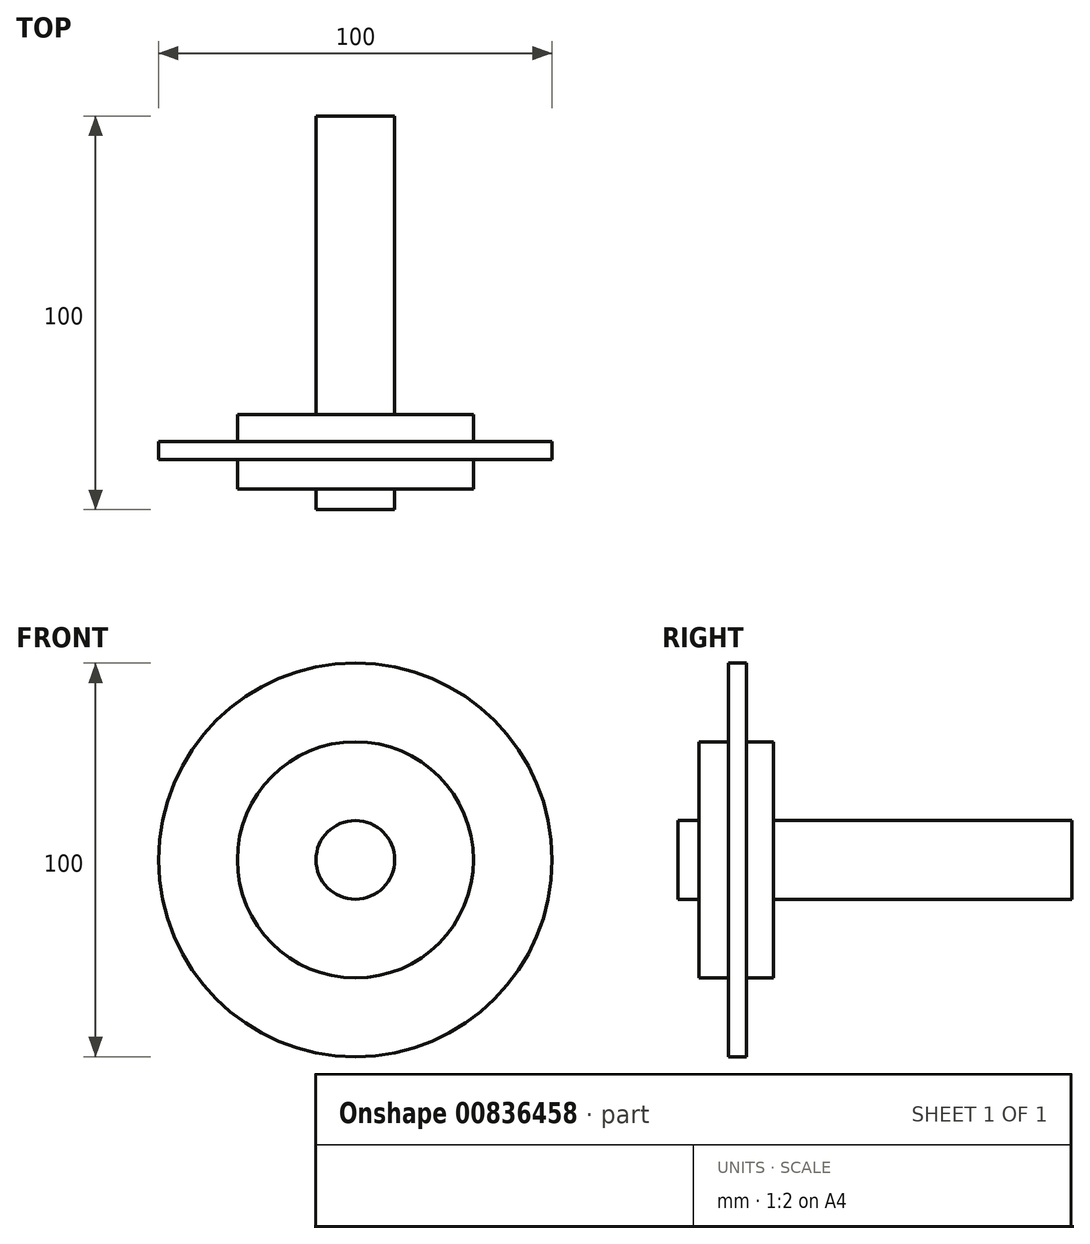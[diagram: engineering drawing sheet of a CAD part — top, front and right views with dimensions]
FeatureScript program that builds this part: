
annotation { "Feature Type Name" : "Feature", "Feature Type Description" : "" }
export const myFeature = defineFeature(function(context is Context, id is Id, definition is map)
    precondition{}
    {
        {
            var Q0;
            Q0=qCreatedBy(makeId("Top.planeOp"),FACE);
            var sketch = newSketch(context, id + "F0", { "sketchPlane" : qUnion([Q0])});
            skLineSegment(sketch, "E0.bottom", {"start": v(0, 0) * mm, "end": v(10, 0) * mm});
            skLineSegment(sketch, "E0.top", {"start": v(0, 100) * mm, "end": v(10, 100) * mm});
            skLineSegment(sketch, "E0.left", {"start": v(0, 0) * mm, "end": v(0, 100) * mm});
            skLineSegment(sketch, "E0.right", {"start": v(10, 0) * mm, "end": v(10, 5.28) * mm});
            skLineSegment(sketch, "E1.bottom", {"start": v(10, 24.16) * mm, "end": v(30, 24.16) * mm});
            skLineSegment(sketch, "E1.top", {"start": v(10, 5.28) * mm, "end": v(30, 5.28) * mm});
            skLineSegment(sketch, "E1.left", {"start": v(0, 24.16) * mm, "end": v(0, 5.28) * mm});
            skLineSegment(sketch, "E1.right", {"start": v(30, 24.16) * mm, "end": v(30, 17.33) * mm});
            skLineSegment(sketch, "E2.bottom", {"start": v(30, 17.33) * mm, "end": v(50, 17.33) * mm});
            skLineSegment(sketch, "E2.top", {"start": v(30, 12.73) * mm, "end": v(50, 12.73) * mm});
            skLineSegment(sketch, "E2.left", {"start": v(0, 17.33) * mm, "end": v(0, 12.73) * mm});
            skLineSegment(sketch, "E2.right", {"start": v(50, 17.33) * mm, "end": v(50, 12.73) * mm});
            skLineSegment(sketch, "E3.trimOffspring", {"start": v(10, 24.16) * mm, "end": v(10, 100) * mm});
            skLineSegment(sketch, "E4.trimOffspring", {"start": v(30, 12.73) * mm, "end": v(30, 5.28) * mm});
            skSolve(sketch);
        }
        {
            var Q0;
            {var subQ5=sQuery(id+"F0.wireOp",EDGE,"E0.bottom");Q0=makeQuery(id+"F0.imprint","IMPRINT",FACE,{"disambiguationData":[TD([[makeQuery(id+"F0.imprint","IMPRINT",EDGE,{"derivedFrom":subQ5}),1.0]])]});}
            var Q1;
            Q1=sQuery(id+"F0.wireOp",EDGE,"E0.left");
            revolve(context, id + "F1", {"surfaceOperationType" : NewSurfaceOperationType.NEW, "entities" : qUnion([Q0]), "axis" : qUnion([Q1]), "revolveType" : RevolveType.FULL});
        }
    });
